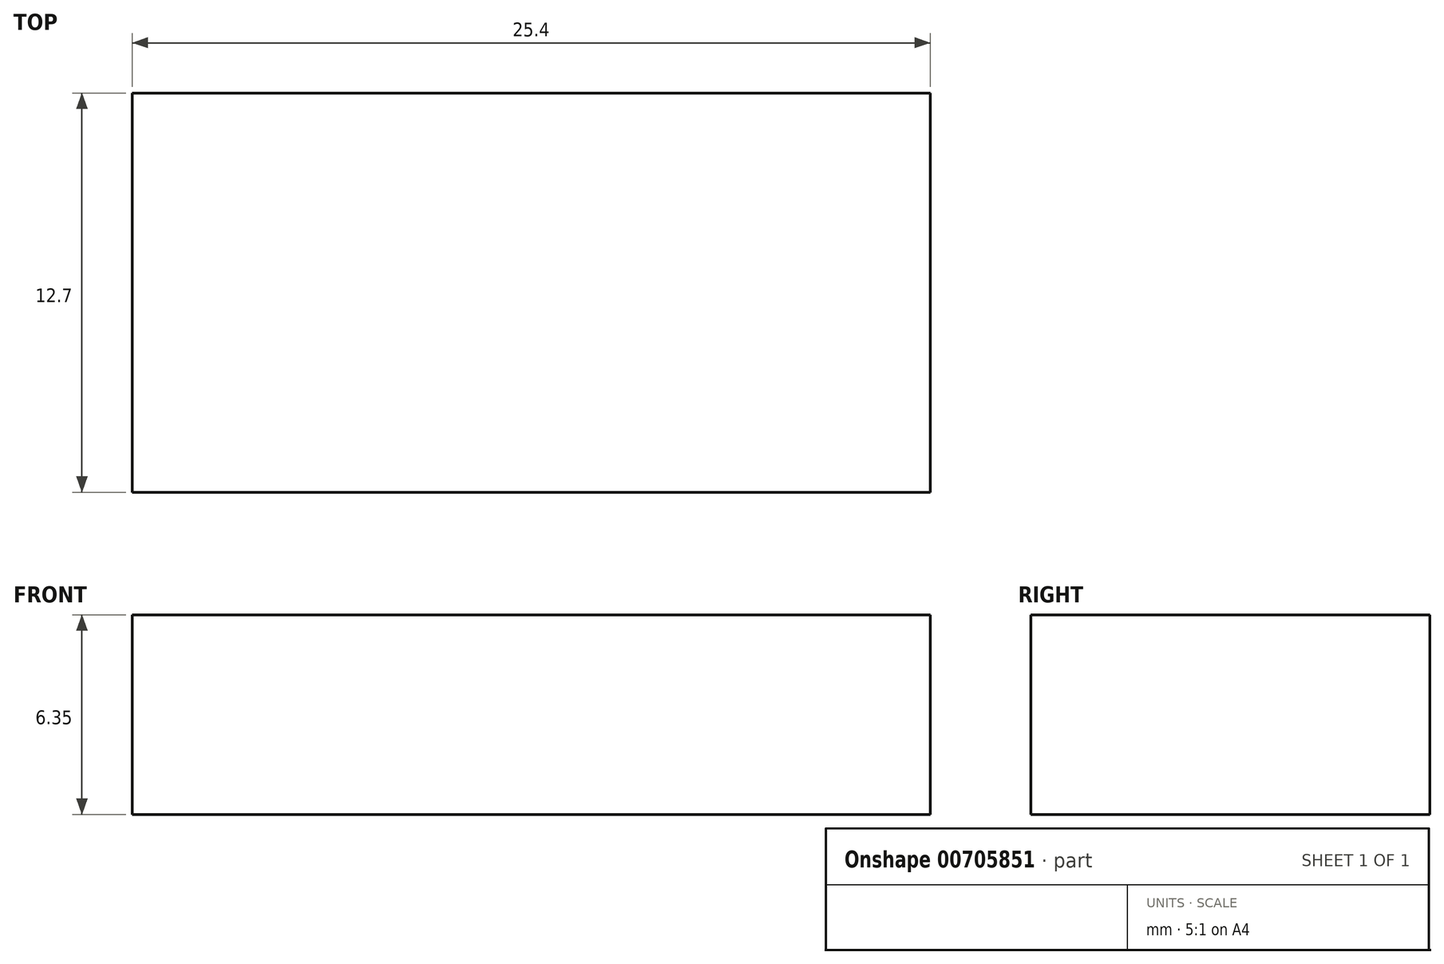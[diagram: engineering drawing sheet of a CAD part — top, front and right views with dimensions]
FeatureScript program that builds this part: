
annotation { "Feature Type Name" : "Feature", "Feature Type Description" : "" }
export const myFeature = defineFeature(function(context is Context, id is Id, definition is map)
    precondition{}
    {
        {
            var Q0;
            Q0=qCreatedBy(makeId("Top.planeOp"),FACE);
            var sketch = newSketch(context, id + "F0", { "sketchPlane" : qUnion([Q0])});
            skLineSegment(sketch, "E0", {"start": v(-91.55, 69.36) * mm, "end": v(111.65, 69.36) * mm});
            skLineSegment(sketch, "E1", {"start": v(111.65, 69.36) * mm, "end": v(111.65, -32.24) * mm});
            skLineSegment(sketch, "E2", {"start": v(111.65, -32.24) * mm, "end": v(-91.55, -32.24) * mm});
            skLineSegment(sketch, "E3", {"start": v(-91.55, -32.24) * mm, "end": v(-91.55, 69.36) * mm});
            skSolve(sketch);
        }
        {
            var Q0;
            Q0 = qSketchRegion(id + "F0", true);
            extrude(context, id + "F1", {"entities" : qUnion([Q0]), "depth" : 50.8 * mm, "offsetDistance" : 25.4 * mm});
        }
        {
            var Q0;
            Q0=qCreatedBy(makeId("Right.planeOp"),FACE);
            var sketch = newSketch(context, id + "F2", { "sketchPlane" : qUnion([Q0])});
            skLineSegment(sketch, "E4", {"start": v(645.63, 127) * mm, "end": v(496.12, 127) * mm});
            skLineSegment(sketch, "E5", {"start": v(496.12, 127) * mm, "end": v(496.12, 113.4) * mm});
            skLineSegment(sketch, "E6", {"start": v(496.12, 127) * mm, "end": v(496.12, 0) * mm});
            skLineSegment(sketch, "E7", {"start": v(496.12, 0) * mm, "end": v(641.75, 0) * mm});
            skLineSegment(sketch, "E8", {"start": v(56.78, 0) * mm, "end": v(56.78, 6.35) * mm});
            skLineSegment(sketch, "E9", {"start": v(56.78, 6.35) * mm, "end": v(69.48, 6.35) * mm});
            skLineSegment(sketch, "E10", {"start": v(69.48, 6.35) * mm, "end": v(69.48, 0) * mm});
            skLineSegment(sketch, "E11", {"start": v(69.48, 0) * mm, "end": v(56.78, 0) * mm});
            skSolve(sketch);
        }
        {
            var Q0;
            Q0=makeQuery(id+"F1.opExtrude","SWEPT_BODY",BODY,{"disambiguationData":[OSD([sQuery(id+"F0.wireOp",EDGE,"E0"),sQuery(id+"F0.wireOp",EDGE,"E1"),sQuery(id+"F0.wireOp",EDGE,"E2"),sQuery(id+"F0.wireOp",EDGE,"E3")])]});
            deleteBodies(context, id + "F3", {"entities" : qUnion([Q0])});
        }
        {
            var Q0;
            Q0=makeQuery(id+"F2.imprint","IMPRINT",FACE,{"disambiguationData":[TD([[makeQuery(id+"F2.imprint","IMPRINT",EDGE,{"derivedFrom":sQuery(id+"F2.wireOp",EDGE,"E8")}),-1.0]])]});
            extrude(context, id + "F4", {"entities" : qUnion([Q0]), "depth" : 25.4 * mm, "offsetDistance" : 25.4 * mm});
        }
    });
